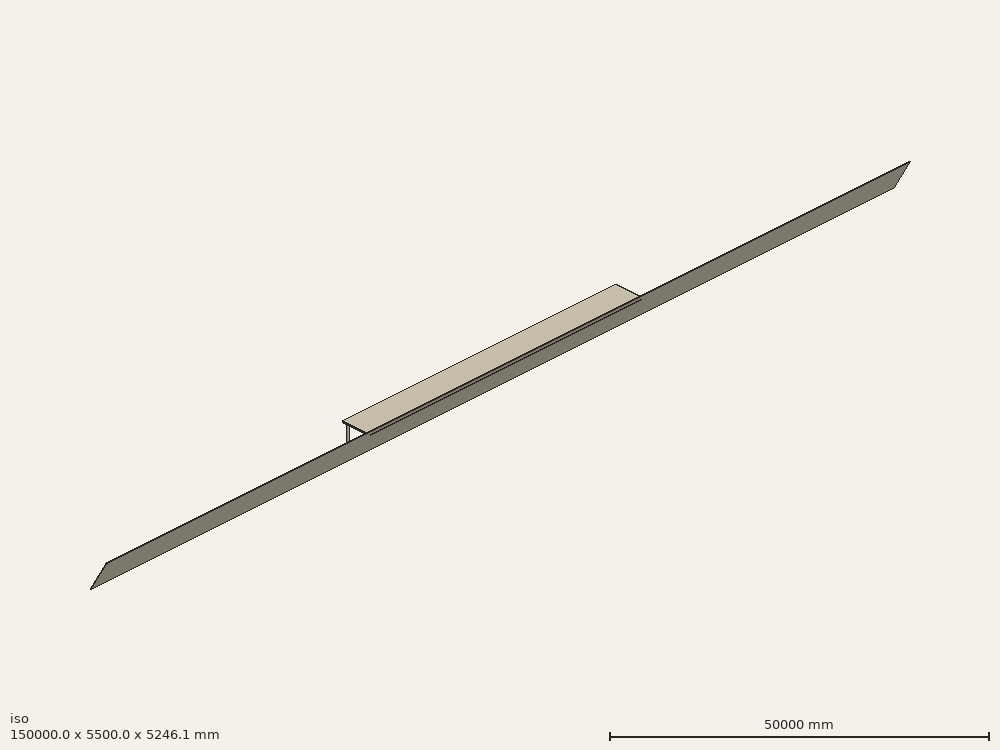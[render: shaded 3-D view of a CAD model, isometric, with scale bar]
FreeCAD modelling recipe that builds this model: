
FCSTD DOCUMENT  (FreeCAD 0.16R6703 (Git))
Label: dock
License: All rights reserved
LicenseURL: http://en.wikipedia.org/wiki/All_rights_reserved
objects: Part::Cylinder×11, Part::Box×2, Part::MultiFuse×1
note: 14 computed .brp shape members not serialized (recipe doc carries the construction recipe); baked Part::Feature solids carry a one-line shape summary decoded from their .brp

FEATURE [Part::Box] Box  label="Cube"
  Height = 300
  Length = 51000
  Placement = pos=(-25500,-5000,200) rot=(0,0,1;0rad)
  Width = 5000
FEATURE [Part::Cylinder] Cylinder
  Angle = 360
  Height = 4000
  Placement = pos=(0,-500,-3800) rot=(0,0,1;0rad)
  Radius = 200
FEATURE [Part::Cylinder] Cylinder001
  Angle = 360
  Height = 4000
  Placement = pos=(5000,-500,-3800) rot=(0,0,1;0rad)
  Radius = 200
FEATURE [Part::Cylinder] Cylinder002
  Angle = 360
  Height = 4000
  Placement = pos=(10000,-500,-3800) rot=(0,0,1;0rad)
  Radius = 200
FEATURE [Part::Cylinder] Cylinder003
  Angle = 360
  Height = 4000
  Placement = pos=(15000,-500,-3800) rot=(0,0,1;0rad)
  Radius = 200
FEATURE [Part::Cylinder] Cylinder004
  Angle = 360
  Height = 4000
  Placement = pos=(20000,-500,-3800) rot=(0,0,1;0rad)
  Radius = 200
FEATURE [Part::Cylinder] Cylinder005
  Angle = 360
  Height = 4000
  Placement = pos=(25000,-500,-3800) rot=(0,0,1;0rad)
  Radius = 200
FEATURE [Part::Cylinder] Cylinder006
  Angle = 360
  Height = 4000
  Placement = pos=(-5000,-500,-3800) rot=(0,0,1;0rad)
  Radius = 200
FEATURE [Part::Cylinder] Cylinder007
  Angle = 360
  Height = 4000
  Placement = pos=(-10000,-500,-3800) rot=(0,0,1;0rad)
  Radius = 200
FEATURE [Part::Cylinder] Cylinder008
  Angle = 360
  Height = 4000
  Placement = pos=(-15000,-500,-3800) rot=(0,0,1;0rad)
  Radius = 200
FEATURE [Part::Cylinder] Cylinder009
  Angle = 360
  Height = 4000
  Placement = pos=(-20000,-500,-3800) rot=(0,0,1;0rad)
  Radius = 200
FEATURE [Part::Cylinder] Cylinder010
  Angle = 360
  Height = 4000
  Placement = pos=(-25000,-500,-3800) rot=(0,0,1;0rad)
  Radius = 200
FEATURE [Part::Box] Box001  label="Cube001"
  Height = 6000
  Length = 150000
  Placement = pos=(-75000,-2500,-4000) rot=(1,0,0;0.523599rad)
  Width = 100
FEATURE [Part::MultiFuse] Fusion
  Shapes = -> [Box,Cylinder010,Cylinder,Cylinder008,Cylinder007,Cylinder005,Cylinder003,Cylinder004,Cylinder002,Cylinder009,Box001,Cylinder001,Cylinder006]
